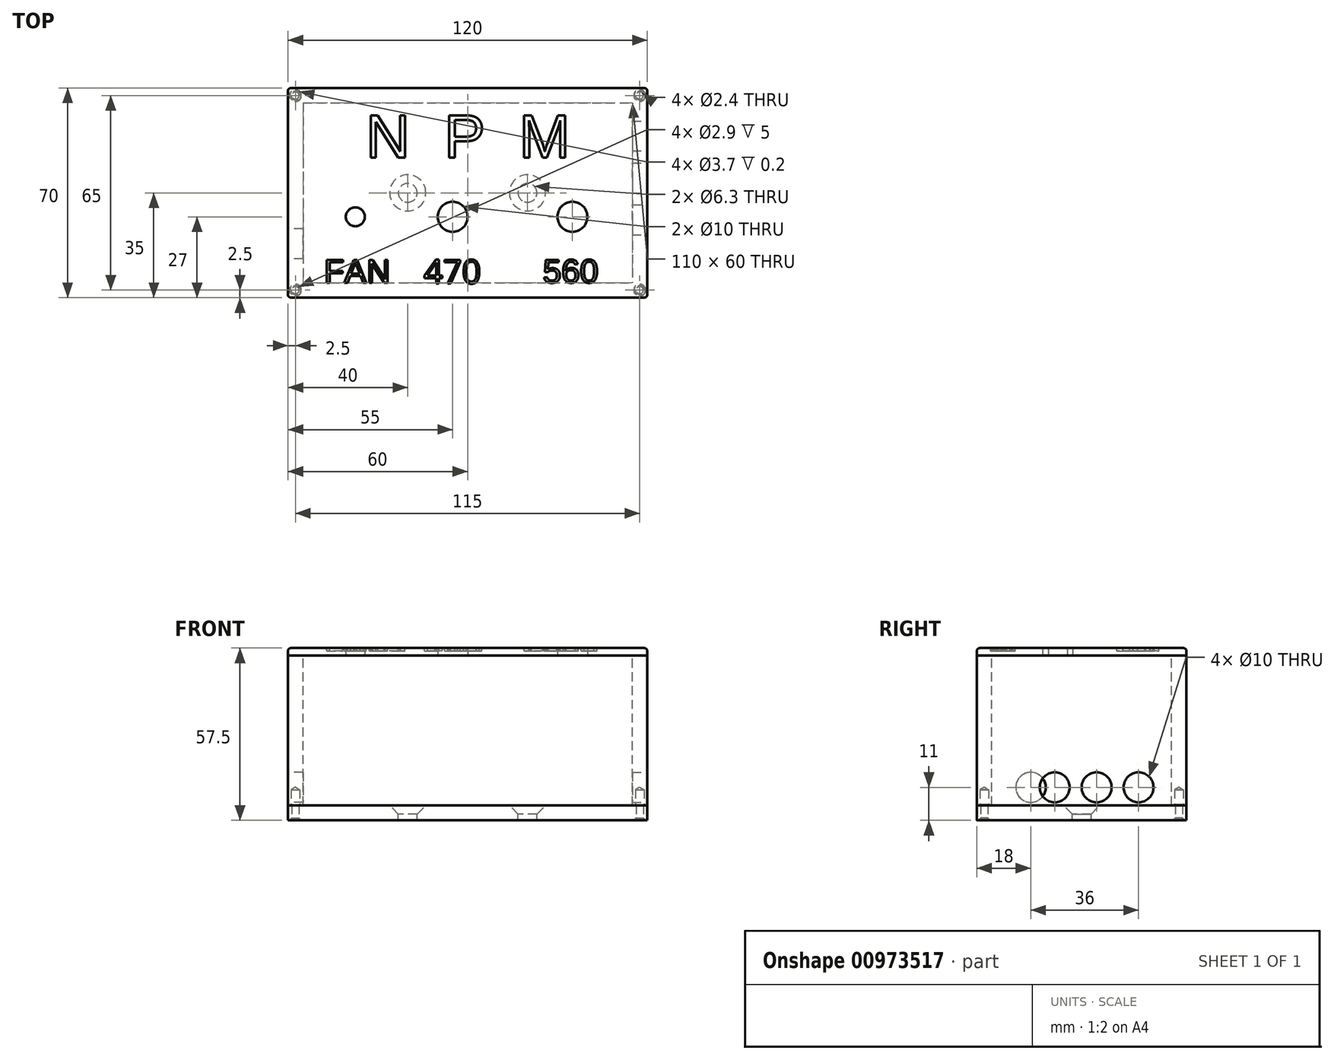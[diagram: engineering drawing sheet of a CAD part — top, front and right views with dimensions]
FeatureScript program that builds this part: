
annotation { "Feature Type Name" : "Feature", "Feature Type Description" : "" }
export const myFeature = defineFeature(function(context is Context, id is Id, definition is map)
    precondition{}
    {
        {
            var Q0;
            Q0=qCreatedBy(makeId("Top.planeOp"),FACE);
            var sketch = newSketch(context, id + "F0", { "sketchPlane" : qUnion([Q0])});
            skLineSegment(sketch, "E0.bottom", {"start": v(0, 0) * mm, "end": v(120, 0) * mm});
            skLineSegment(sketch, "E0.top", {"start": v(0, 70) * mm, "end": v(120, 70) * mm});
            skLineSegment(sketch, "E0.left", {"start": v(0, 0) * mm, "end": v(0, 70) * mm});
            skLineSegment(sketch, "E0.right", {"start": v(120, 0) * mm, "end": v(120, 70) * mm});
            skCircle(sketch, "E1", {"center": v(95, 27) * mm, "radius": 5 * mm});
            skCircle(sketch, "E2", {"center": v(55, 27) * mm, "radius": 5 * mm});
            skCircle(sketch, "E3", {"center": v(22.5, 27) * mm, "radius": 3.18 * mm});
            skLineSegment(sketch, "E4", {"start": v(5, 70) * mm, "end": v(5, 5) * mm, "construction": true});
            skLineSegment(sketch, "E5", {"start": v(5, 5) * mm, "end": v(115, 5) * mm, "construction": true});
            skLineSegment(sketch, "E6", {"start": v(115, 5) * mm, "end": v(115, 70) * mm, "construction": true});
            skLineSegment(sketch, "E7", {"start": v(0, 65) * mm, "end": v(120, 65) * mm, "construction": true});
            skLineSegment(sketch, "E8", {"start": v(5, 5) * mm, "end": v(0, 5) * mm, "construction": true});
            skLineSegment(sketch, "E9", {"start": v(115, 5) * mm, "end": v(120, 5) * mm, "construction": true});
            skPoint(sketch, "E10.endSnap0", {"position": v(5, 37.5) * mm});
            skLineSegment(sketch, "E11", {"start": v(5, 70) * mm, "end": v(115, 65) * mm, "construction": true});
            skLineSegment(sketch, "E12", {"start": v(115, 70) * mm, "end": v(5, 65) * mm, "construction": true});
            skLineSegment(sketch, "E13", {"start": v(120, 5) * mm, "end": v(0, 0) * mm, "construction": true});
            skLineSegment(sketch, "E14", {"start": v(0, 5) * mm, "end": v(120, 0) * mm, "construction": true});
            skPoint(sketch, "E15", {"position": v(60, 2.5) * mm});
            skPoint(sketch, "E16", {"position": v(60, 67.5) * mm});
            skLineSegment(sketch, "E17", {"start": v(5, 27) * mm, "end": v(115, 27) * mm, "construction": true});
            skSolve(sketch);
        }
        {
            var Q0;
            Q0=makeQuery(id+"F0.imprint","IMPRINT",FACE,{"disambiguationData":[TD([[makeQuery(id+"F0.imprint","IMPRINT",EDGE,{"derivedFrom":sQuery(id+"F0.wireOp",EDGE,"E0.bottom")}),1.0]])]});
            extrude(context, id + "F1", {"entities" : qUnion([Q0]), "depth" : 2.5 * mm, "offsetDistance" : 25 * mm});
        }
        {
            var Q0;
            Q0=makeQuery(id+"F1.opExtrude","CAP_FACE",FACE,{"disambiguationData":[OSD([sQuery(id+"F0.wireOp",EDGE,"E0.bottom"),sQuery(id+"F0.wireOp",EDGE,"E0.top"),sQuery(id+"F0.wireOp",EDGE,"E0.left"),sQuery(id+"F0.wireOp",EDGE,"E0.right"),sQuery(id+"F0.wireOp",EDGE,"E1"),sQuery(id+"F0.wireOp",EDGE,"E2"),sQuery(id+"F0.wireOp",EDGE,"E3")])],"isStart":true});
            var sketch = newSketch(context, id + "F2", { "sketchPlane" : qUnion([Q0])});
            skLineSegment(sketch, "E18.bottom", {"start": v(0, -70) * mm, "end": v(120, -70) * mm, "construction": true});
            skLineSegment(sketch, "E18.top", {"start": v(0, 0) * mm, "end": v(120, 0) * mm, "construction": true});
            skLineSegment(sketch, "E18.left", {"start": v(0, -70) * mm, "end": v(0, 0) * mm, "construction": true});
            skLineSegment(sketch, "E18.right", {"start": v(120, -70) * mm, "end": v(120, 0) * mm, "construction": true});
            skLineSegment(sketch, "E19.bottom", {"start": v(5, -65) * mm, "end": v(115, -65) * mm});
            skLineSegment(sketch, "E19.top", {"start": v(5, -5) * mm, "end": v(115, -5) * mm});
            skLineSegment(sketch, "E19.left", {"start": v(5, -65) * mm, "end": v(5, -5) * mm});
            skLineSegment(sketch, "E19.right", {"start": v(115, -65) * mm, "end": v(115, -5) * mm});
            skSolve(sketch);
        }
        {
            var Q0;
            Q0=makeQuery(id+"F2.imprint","IMPRINT",FACE,{"disambiguationData":[TD([[makeQuery(id+"F2.imprint","IMPRINT",EDGE,{"derivedFrom":sQuery(id+"F2.wireOp",EDGE,"E19.bottom")}),-1.0]])]});
            var Q1;
            Q1=makeQuery(id+"F2.imprint","IMPRINT",FACE,{"disambiguationData":[TD([[makeQuery(id+"F2.imprint","IMPRINT",EDGE,{"derivedFrom":makeQuery(id+"FxvTJw6m9mzOm3c_1.hole-0.boolean.opBoolean","INTERSECT",EDGE,{"derivedFrom":[makeQuery(id+"F1.opExtrude","CAP_FACE",FACE,{"disambiguationData":[OSD([sQuery(id+"F0.wireOp",EDGE,"E0.bottom"),sQuery(id+"F0.wireOp",EDGE,"E0.top"),sQuery(id+"F0.wireOp",EDGE,"E0.left"),sQuery(id+"F0.wireOp",EDGE,"E0.right"),sQuery(id+"F0.wireOp",EDGE,"E1"),sQuery(id+"F0.wireOp",EDGE,"E2"),sQuery(id+"F0.wireOp",EDGE,"E3")])],"isStart":true}),makeQuery(id+"FxvTJw6m9mzOm3c_1.hole-0.opRevolve","SWEPT_FACE",FACE,{"disambiguationData":[OSD([sQuery(id+"FxvTJw6m9mzOm3c_1.hole-0.sketch.wireOp",EDGE,"core_line_2")])]})]})}),1.0]])]});
            var Q2;
            Q2=makeQuery(id+"F2.imprint","IMPRINT",FACE,{"disambiguationData":[TD([[makeQuery(id+"F2.imprint","IMPRINT",EDGE,{"derivedFrom":makeQuery(id+"FxvTJw6m9mzOm3c_1.hole-1.boolean.opBoolean","INTERSECT",EDGE,{"derivedFrom":[makeQuery(id+"F1.opExtrude","CAP_FACE",FACE,{"disambiguationData":[OSD([sQuery(id+"F0.wireOp",EDGE,"E0.bottom"),sQuery(id+"F0.wireOp",EDGE,"E0.top"),sQuery(id+"F0.wireOp",EDGE,"E0.left"),sQuery(id+"F0.wireOp",EDGE,"E0.right"),sQuery(id+"F0.wireOp",EDGE,"E1"),sQuery(id+"F0.wireOp",EDGE,"E2"),sQuery(id+"F0.wireOp",EDGE,"E3")])],"isStart":true}),makeQuery(id+"FxvTJw6m9mzOm3c_1.hole-1.opRevolve","SWEPT_FACE",FACE,{"disambiguationData":[OSD([sQuery(id+"FxvTJw6m9mzOm3c_1.hole-1.sketch.wireOp",EDGE,"core_line_2")])]})]})}),1.0]])]});
            var Q3;
            Q3=makeQuery(id+"F2.imprint","IMPRINT",FACE,{"disambiguationData":[TD([[makeQuery(id+"F2.imprint","IMPRINT",EDGE,{"derivedFrom":makeQuery(id+"FxvTJw6m9mzOm3c_1.hole-2.boolean.opBoolean","INTERSECT",EDGE,{"derivedFrom":[makeQuery(id+"F1.opExtrude","CAP_FACE",FACE,{"disambiguationData":[OSD([sQuery(id+"F0.wireOp",EDGE,"E0.bottom"),sQuery(id+"F0.wireOp",EDGE,"E0.top"),sQuery(id+"F0.wireOp",EDGE,"E0.left"),sQuery(id+"F0.wireOp",EDGE,"E0.right"),sQuery(id+"F0.wireOp",EDGE,"E1"),sQuery(id+"F0.wireOp",EDGE,"E2"),sQuery(id+"F0.wireOp",EDGE,"E3")])],"isStart":true}),makeQuery(id+"FxvTJw6m9mzOm3c_1.hole-2.opRevolve","SWEPT_FACE",FACE,{"disambiguationData":[OSD([sQuery(id+"FxvTJw6m9mzOm3c_1.hole-2.sketch.wireOp",EDGE,"core_line_2")])]})]})}),1.0]])]});
            var Q4;
            Q4=makeQuery(id+"F2.imprint","IMPRINT",FACE,{"disambiguationData":[TD([[makeQuery(id+"F2.imprint","IMPRINT",EDGE,{"derivedFrom":makeQuery(id+"FxvTJw6m9mzOm3c_1.hole-3.boolean.opBoolean","INTERSECT",EDGE,{"derivedFrom":[makeQuery(id+"F1.opExtrude","CAP_FACE",FACE,{"disambiguationData":[OSD([sQuery(id+"F0.wireOp",EDGE,"E0.bottom"),sQuery(id+"F0.wireOp",EDGE,"E0.top"),sQuery(id+"F0.wireOp",EDGE,"E0.left"),sQuery(id+"F0.wireOp",EDGE,"E0.right"),sQuery(id+"F0.wireOp",EDGE,"E1"),sQuery(id+"F0.wireOp",EDGE,"E2"),sQuery(id+"F0.wireOp",EDGE,"E3")])],"isStart":true}),makeQuery(id+"FxvTJw6m9mzOm3c_1.hole-3.opRevolve","SWEPT_FACE",FACE,{"disambiguationData":[OSD([sQuery(id+"FxvTJw6m9mzOm3c_1.hole-3.sketch.wireOp",EDGE,"core_line_2")])]})]})}),1.0]])]});
            extrude(context, id + "F3", {"entities" : qUnion([Q0, Q1, Q2, Q3, Q4]), "depth" : 50 * mm, "offsetDistance" : 25 * mm});
        }
        {
            var Q0;
            Q0=makeQuery(id+"F3.opExtrude","CAP_FACE",FACE,{"disambiguationData":[OSD([sQuery(id+"F0.wireOp",EDGE,"E0.bottom"),sQuery(id+"F0.wireOp",EDGE,"E0.top"),sQuery(id+"F0.wireOp",EDGE,"E0.left"),sQuery(id+"F0.wireOp",EDGE,"E0.right"),sQuery(id+"F2.wireOp",EDGE,"E19.bottom"),sQuery(id+"F2.wireOp",EDGE,"E19.top"),sQuery(id+"F2.wireOp",EDGE,"E19.left"),sQuery(id+"F2.wireOp",EDGE,"E19.right")])],"isStart":false});
            var sketch = newSketch(context, id + "F4", { "sketchPlane" : qUnion([Q0])});
            skLineSegment(sketch, "E20.bottom", {"start": v(0, 0) * mm, "end": v(120, 0) * mm});
            skLineSegment(sketch, "E20.top", {"start": v(0, -70) * mm, "end": v(120, -70) * mm});
            skLineSegment(sketch, "E20.left", {"start": v(0, 0) * mm, "end": v(0, -70) * mm});
            skLineSegment(sketch, "E20.right", {"start": v(120, 0) * mm, "end": v(120, -70) * mm});
            skLineSegment(sketch, "E21.bottom", {"start": v(5, -5) * mm, "end": v(115, -5) * mm, "construction": true});
            skLineSegment(sketch, "E21.top", {"start": v(5, -65) * mm, "end": v(115, -65) * mm, "construction": true});
            skLineSegment(sketch, "E21.left", {"start": v(5, -5) * mm, "end": v(5, -65) * mm, "construction": true});
            skLineSegment(sketch, "E21.right", {"start": v(115, -5) * mm, "end": v(115, -65) * mm, "construction": true});
            skSolve(sketch);
        }
        {
            var Q0;
            Q0=makeQuery(id+"F4.imprint","IMPRINT",FACE,{"disambiguationData":[TD([[makeQuery(id+"F4.imprint","IMPRINT",EDGE,{"derivedFrom":sQuery(id+"F4.wireOp",EDGE,"E20.bottom")}),-1.0]])]});
            var Q1;
            Q1=makeQuery(id+"F4.imprint","IMPRINT",FACE,{"disambiguationData":[TD([[makeQuery(id+"F4.imprint","IMPRINT",EDGE,{"derivedFrom":makeQuery(id+"F3.opExtrude","CAP_EDGE",EDGE,{"disambiguationData":[OSD([sQuery(id+"F2.wireOp",EDGE,"E19.bottom")])],"isStart":false})}),1.0]])]});
            extrude(context, id + "F5", {"entities" : qUnion([Q0, Q1]), "depth" : 5 * mm, "offsetDistance" : 25 * mm});
        }
        {
            var Q0;
            Q0=makeQuery(id+"F5.opExtrude","CAP_FACE",FACE,{"disambiguationData":[OSD([sQuery(id+"F4.wireOp",EDGE,"E20.bottom"),sQuery(id+"F4.wireOp",EDGE,"E20.top"),sQuery(id+"F4.wireOp",EDGE,"E20.left"),sQuery(id+"F4.wireOp",EDGE,"E20.right")])],"isStart":false});
            var sketch = newSketch(context, id + "F6", { "sketchPlane" : qUnion([Q0])});
            skLineSegment(sketch, "E22.bottom", {"start": v(0, -70) * mm, "end": v(120, -70) * mm, "construction": true});
            skLineSegment(sketch, "E22.top", {"start": v(0, 0) * mm, "end": v(120, 0) * mm, "construction": true});
            skLineSegment(sketch, "E22.left", {"start": v(0, -70) * mm, "end": v(0, 0) * mm, "construction": true});
            skLineSegment(sketch, "E22.right", {"start": v(120, -70) * mm, "end": v(120, 0) * mm, "construction": true});
            skLineSegment(sketch, "E23.bottom", {"start": v(5, -65) * mm, "end": v(115, -65) * mm, "construction": true});
            skLineSegment(sketch, "E23.top", {"start": v(5, -5) * mm, "end": v(115, -5) * mm, "construction": true});
            skLineSegment(sketch, "E23.left", {"start": v(5, -65) * mm, "end": v(5, -5) * mm, "construction": true});
            skLineSegment(sketch, "E23.right", {"start": v(115, -65) * mm, "end": v(115, -5) * mm, "construction": true});
            skLineSegment(sketch, "E24", {"start": v(5, -5) * mm, "end": v(0, 0) * mm, "construction": true});
            skLineSegment(sketch, "E25", {"start": v(115, -5) * mm, "end": v(120, 0) * mm, "construction": true});
            skLineSegment(sketch, "E26", {"start": v(115, -65) * mm, "end": v(120, -70) * mm, "construction": true});
            skLineSegment(sketch, "E27", {"start": v(5, -65) * mm, "end": v(0, -70) * mm, "construction": true});
            skPoint(sketch, "E28", {"position": v(2.5, -2.5) * mm});
            skPoint(sketch, "E29", {"position": v(117.5, -2.5) * mm});
            skPoint(sketch, "E30", {"position": v(117.5, -67.5) * mm});
            skPoint(sketch, "E31", {"position": v(2.5, -67.5) * mm});
            skSolve(sketch);
        }
        {
            var Q0;
            Q0=sQuery(id+"F6.wireOp",VERTEX,"E28");
            var Q1;
            Q1=sQuery(id+"F6.wireOp",VERTEX,"E31");
            var Q2;
            Q2=sQuery(id+"F6.wireOp",VERTEX,"E30");
            var Q3;
            Q3=sQuery(id+"F6.wireOp",VERTEX,"E29");
            var Q4;
            Q4=makeQuery(id+"F3.opExtrude","SWEPT_BODY",BODY,{"disambiguationData":[OSD([sQuery(id+"F0.wireOp",EDGE,"E0.bottom"),sQuery(id+"F0.wireOp",EDGE,"E0.top"),sQuery(id+"F0.wireOp",EDGE,"E0.left"),sQuery(id+"F0.wireOp",EDGE,"E0.right"),sQuery(id+"F2.wireOp",EDGE,"E19.bottom"),sQuery(id+"F2.wireOp",EDGE,"E19.top"),sQuery(id+"F2.wireOp",EDGE,"E19.left"),sQuery(id+"F2.wireOp",EDGE,"E19.right")])]});
            var Q5;
            Q5=makeQuery(id+"F5.opExtrude","SWEPT_BODY",BODY,{"disambiguationData":[OSD([sQuery(id+"F4.wireOp",EDGE,"E20.bottom"),sQuery(id+"F4.wireOp",EDGE,"E20.top"),sQuery(id+"F4.wireOp",EDGE,"E20.left"),sQuery(id+"F4.wireOp",EDGE,"E20.right")])]});
            hole(context, id + "F7", {"style" : HoleStyle.C_SINK, "endStyle" : HoleEndStyle.BLIND, "holeDiameter" : 2.4 * mm, "cSinkDiameter" : 4 * mm, "cSinkAngle" : 90 * degree, "majorDiameter" : 5 * mm, "holeDepth" : 5 * mm, "isTappedThrough" : true, "tappedDepth" : 12 * mm, "tapClearance" : 3, "locations" : qUnion([Q0, Q1, Q2, Q3]), "scope" : qUnion([Q4, Q5])});
        }
        {
            var Q0;
            Q0=makeQuery(id+"F3.opExtrude","CAP_FACE",FACE,{"disambiguationData":[OSD([sQuery(id+"F0.wireOp",EDGE,"E0.bottom"),sQuery(id+"F0.wireOp",EDGE,"E0.top"),sQuery(id+"F0.wireOp",EDGE,"E0.left"),sQuery(id+"F0.wireOp",EDGE,"E0.right"),sQuery(id+"F2.wireOp",EDGE,"E19.bottom"),sQuery(id+"F2.wireOp",EDGE,"E19.top"),sQuery(id+"F2.wireOp",EDGE,"E19.left"),sQuery(id+"F2.wireOp",EDGE,"E19.right")])],"isStart":false});
            var sketch = newSketch(context, id + "F8", { "sketchPlane" : qUnion([Q0])});
            skPoint(sketch, "E32", {"position": v(2.5, -2.5) * mm});
            skPoint(sketch, "E33", {"position": v(2.5, -67.5) * mm});
            skPoint(sketch, "E34", {"position": v(117.5, -67.5) * mm});
            skPoint(sketch, "E35", {"position": v(117.5, -2.5) * mm});
            skSolve(sketch);
        }
        {
            var Q0;
            Q0=sQuery(id+"F8.wireOp",VERTEX,"E32");
            var Q1;
            Q1=sQuery(id+"F8.wireOp",VERTEX,"E33");
            var Q2;
            Q2=sQuery(id+"F8.wireOp",VERTEX,"E34");
            var Q3;
            Q3=sQuery(id+"F8.wireOp",VERTEX,"E35");
            var Q4;
            Q4=makeQuery(id+"F3.opExtrude","SWEPT_BODY",BODY,{"disambiguationData":[OSD([sQuery(id+"F0.wireOp",EDGE,"E0.bottom"),sQuery(id+"F0.wireOp",EDGE,"E0.top"),sQuery(id+"F0.wireOp",EDGE,"E0.left"),sQuery(id+"F0.wireOp",EDGE,"E0.right"),sQuery(id+"F2.wireOp",EDGE,"E19.bottom"),sQuery(id+"F2.wireOp",EDGE,"E19.top"),sQuery(id+"F2.wireOp",EDGE,"E19.left"),sQuery(id+"F2.wireOp",EDGE,"E19.right")])]});
            hole(context, id + "F9", {"style" : HoleStyle.C_BORE, "endStyle" : HoleEndStyle.BLIND, "holeDiameter" : 2.9 * mm, "cBoreDiameter" : 3.7 * mm, "cBoreDepth" : .2 * mm, "majorDiameter" : 5 * mm, "holeDepth" : 5.2 * mm, "isTappedThrough" : true, "tappedDepth" : 12 * mm, "tapClearance" : 3, "locations" : qUnion([Q0, Q1, Q2, Q3]), "scope" : qUnion([Q4])});
        }
        {
            var Q0;
            Q0=makeQuery(id+"F1.opExtrude","CAP_EDGE",EDGE,{"disambiguationData":[OSD([sQuery(id+"F0.wireOp",EDGE,"E0.bottom")])],"isStart":false});
            var Q1;
            Q1=makeQuery(id+"F1.opExtrude","CAP_EDGE",EDGE,{"disambiguationData":[OSD([sQuery(id+"F0.wireOp",EDGE,"E0.left")])],"isStart":false});
            var Q2;
            Q2=makeQuery(id+"F1.opExtrude","CAP_EDGE",EDGE,{"disambiguationData":[OSD([sQuery(id+"F0.wireOp",EDGE,"E0.top")])],"isStart":false});
            var Q3;
            Q3=makeQuery(id+"F1.opExtrude","CAP_EDGE",EDGE,{"disambiguationData":[OSD([sQuery(id+"F0.wireOp",EDGE,"E0.right")])],"isStart":false});
            var Q4;
            Q4=makeQuery(id+"F3.opExtrude","SWEPT_EDGE",EDGE,{"disambiguationData":[OSD([sQuery(id+"F0.wireOp",EDGE,"E0.bottom"),sQuery(id+"F0.wireOp",EDGE,"E0.right")])]});
            var Q5;
            Q5=makeQuery(id+"F3.opExtrude","SWEPT_EDGE",EDGE,{"disambiguationData":[OSD([sQuery(id+"F0.wireOp",EDGE,"E0.bottom"),sQuery(id+"F0.wireOp",EDGE,"E0.left")])]});
            var Q6;
            Q6=makeQuery(id+"F1.opExtrude","SWEPT_EDGE",EDGE,{"disambiguationData":[OSD([sQuery(id+"F0.wireOp",EDGE,"E0.bottom"),sQuery(id+"F0.wireOp",EDGE,"E0.left")])]});
            var Q7;
            Q7=makeQuery(id+"F1.opExtrude","SWEPT_EDGE",EDGE,{"disambiguationData":[OSD([sQuery(id+"F0.wireOp",EDGE,"E0.bottom"),sQuery(id+"F0.wireOp",EDGE,"E0.right")])]});
            var Q8;
            Q8=makeQuery(id+"F3.opExtrude","SWEPT_EDGE",EDGE,{"disambiguationData":[OSD([sQuery(id+"F0.wireOp",EDGE,"E0.top"),sQuery(id+"F0.wireOp",EDGE,"E0.right")])]});
            var Q9;
            Q9=makeQuery(id+"F1.opExtrude","SWEPT_EDGE",EDGE,{"disambiguationData":[OSD([sQuery(id+"F0.wireOp",EDGE,"E0.top"),sQuery(id+"F0.wireOp",EDGE,"E0.right")])]});
            var Q10;
            Q10=makeQuery(id+"F3.opExtrude","SWEPT_EDGE",EDGE,{"disambiguationData":[OSD([sQuery(id+"F0.wireOp",EDGE,"E0.top"),sQuery(id+"F0.wireOp",EDGE,"E0.left")])]});
            var Q11;
            Q11=makeQuery(id+"F1.opExtrude","SWEPT_EDGE",EDGE,{"disambiguationData":[OSD([sQuery(id+"F0.wireOp",EDGE,"E0.top"),sQuery(id+"F0.wireOp",EDGE,"E0.left")])]});
            var Q12;
            Q12=makeQuery(id+"F5.opExtrude","SWEPT_EDGE",EDGE,{"disambiguationData":[OSD([sQuery(id+"F4.wireOp",EDGE,"E20.top"),sQuery(id+"F4.wireOp",EDGE,"E20.left")])]});
            var Q13;
            Q13=makeQuery(id+"F5.opExtrude","SWEPT_EDGE",EDGE,{"disambiguationData":[OSD([sQuery(id+"F4.wireOp",EDGE,"E20.bottom"),sQuery(id+"F4.wireOp",EDGE,"E20.left")])]});
            var Q14;
            Q14=makeQuery(id+"F5.opExtrude","SWEPT_EDGE",EDGE,{"disambiguationData":[OSD([sQuery(id+"F4.wireOp",EDGE,"E20.top"),sQuery(id+"F4.wireOp",EDGE,"E20.right")])]});
            var Q15;
            Q15=makeQuery(id+"F5.opExtrude","SWEPT_EDGE",EDGE,{"disambiguationData":[OSD([sQuery(id+"F4.wireOp",EDGE,"E20.bottom"),sQuery(id+"F4.wireOp",EDGE,"E20.right")])]});
            fillet(context, id + "F10", {"entities" : qUnion([Q0, Q1, Q2, Q3, Q4, Q5, Q6, Q7, Q8, Q9, Q10, Q11, Q12, Q13, Q14, Q15]), "radius" : 1 * mm, "tangentPropagation" : true, "allowEdgeOverflow" : false});
        }
        {
            var Q0;
            Q0=makeQuery(id+"F3.opExtrude","SWEPT_FACE",FACE,{"disambiguationData":[OSD([sQuery(id+"F0.wireOp",EDGE,"E0.left")])]});
            var sketch = newSketch(context, id + "F11", { "sketchPlane" : qUnion([Q0])});
            skCircle(sketch, "E36", {"center": v(-18, -44) * mm, "radius": 5 * mm});
            skLineSegment(sketch, "E37", {"start": v(-35, -50) * mm, "end": v(-35, 0) * mm, "construction": true});
            skLineSegment(sketch, "E38", {"start": v(-35, 0) * mm, "end": v(-1, -50) * mm, "construction": true});
            skLineSegment(sketch, "E39", {"start": v(-18, -25) * mm, "end": v(-18, -50) * mm, "construction": true});
            skLineSegment(sketch, "E40", {"start": v(-18, -50) * mm, "end": v(-18, 0) * mm, "construction": true});
            skSolve(sketch);
        }
        {
            var Q0;
            Q0=makeQuery(id+"F11.imprint","IMPRINT",FACE,{"disambiguationData":[TD([[makeQuery(id+"F11.imprint","IMPRINT",EDGE,{"derivedFrom":sQuery(id+"F11.wireOp",EDGE,"E36")}),1.0]])]});
            extrude(context, id + "F12", {"entities" : qUnion([Q0]), "operationType" : NewBodyOperationType.REMOVE, "endBound" : BoundingType.UP_TO_NEXT, "oppositeDirection" : true, "depth" : 25 * mm, "offsetDistance" : 25 * mm});
        }
        {
            var Q0;
            Q0=makeQuery(id+"F3.opExtrude","SWEPT_FACE",FACE,{"disambiguationData":[OSD([sQuery(id+"F0.wireOp",EDGE,"E0.right")])]});
            var sketch = newSketch(context, id + "F13", { "sketchPlane" : qUnion([Q0])});
            skLineSegment(sketch, "E41", {"start": v(1, -44) * mm, "end": v(69, -44) * mm, "construction": true});
            skCircle(sketch, "E42", {"center": v(26, -44) * mm, "radius": 5 * mm});
            skCircle(sketch, "E43", {"center": v(40, -44) * mm, "radius": 5 * mm});
            skCircle(sketch, "E44", {"center": v(54, -44) * mm, "radius": 5 * mm});
            skSolve(sketch);
        }
        {
            var Q0;
            Q0=makeQuery(id+"F13.imprint","IMPRINT",FACE,{"disambiguationData":[TD([[makeQuery(id+"F13.imprint","IMPRINT",EDGE,{"derivedFrom":sQuery(id+"F13.wireOp",EDGE,"E42")}),1.0]])]});
            var Q1;
            Q1=makeQuery(id+"F13.imprint","IMPRINT",FACE,{"disambiguationData":[TD([[makeQuery(id+"F13.imprint","IMPRINT",EDGE,{"derivedFrom":sQuery(id+"F13.wireOp",EDGE,"E43")}),1.0]])]});
            var Q2;
            Q2=makeQuery(id+"F13.imprint","IMPRINT",FACE,{"disambiguationData":[TD([[makeQuery(id+"F13.imprint","IMPRINT",EDGE,{"derivedFrom":sQuery(id+"F13.wireOp",EDGE,"E44")}),1.0]])]});
            extrude(context, id + "F14", {"entities" : qUnion([Q0, Q1, Q2]), "operationType" : NewBodyOperationType.REMOVE, "endBound" : BoundingType.UP_TO_NEXT, "oppositeDirection" : true, "depth" : 25 * mm, "offsetDistance" : 25 * mm});
        }
        {
            var Q0;
            Q0=makeQuery(id+"F10.opFillet","SPLIT",FACE,{"disambiguationData":[OD(4.0)],"derivedFrom":makeQuery(id+"F1.opExtrude","CAP_FACE",FACE,{"disambiguationData":[OSD([sQuery(id+"F0.wireOp",EDGE,"E0.bottom"),sQuery(id+"F0.wireOp",EDGE,"E0.top"),sQuery(id+"F0.wireOp",EDGE,"E0.left"),sQuery(id+"F0.wireOp",EDGE,"E0.right"),sQuery(id+"F0.wireOp",EDGE,"E1"),sQuery(id+"F0.wireOp",EDGE,"E2"),sQuery(id+"F0.wireOp",EDGE,"E3")])],"isStart":false})});
            var sketch = newSketch(context, id + "F15", { "sketchPlane" : qUnion([Q0])});
            skLineSegment(sketch, "E45.bottom", {"start": v(1, 61.5) * mm, "end": v(119, 61.5) * mm, "construction": true});
            skLineSegment(sketch, "E45.top", {"start": v(1, 46.75) * mm, "end": v(119, 46.75) * mm, "construction": true});
            skLineSegment(sketch, "E45.left", {"start": v(1, 61.5) * mm, "end": v(1, 46.75) * mm, "construction": true});
            skLineSegment(sketch, "E45.right", {"start": v(119, 61.5) * mm, "end": v(119, 46.75) * mm, "construction": true});
            skLineSegment(sketch, "E46", {"start": v(60, 61.5) * mm, "end": v(60, 46.75) * mm, "construction": true});
            skLineSegment(sketch, "E47.bottom", {"start": v(77.87, 61.5) * mm, "end": v(25.99, 61.5) * mm, "construction": true});
            skLineSegment(sketch, "E47.top", {"start": v(94.01, 46.75) * mm, "end": v(42.13, 46.75) * mm, "construction": true});
            skLineSegment(sketch, "E47.left", {"start": v(77.87, 61.5) * mm, "end": v(94.01, 46.75) * mm, "construction": true});
            skLineSegment(sketch, "E47.right", {"start": v(25.99, 61.5) * mm, "end": v(42.13, 46.75) * mm, "construction": true});
            skPoint(sketch, "E47.middle", {"position": v(60, 54.12) * mm});
            skText(sketch, "E48", { "text": "N  P  M", "fontName": "Arimo-Regular.ttf"});
            const initialGuessF15  = {"E48": [0.02599, 0.04675, 1, 0, 0.01475]};
            skSetInitialGuess(sketch, initialGuessF15);
            skSolve(sketch);
        }
        {
            var Q0;
            Q0 = qSketchRegion(id + "F15", true);
            extrude(context, id + "F16", {"entities" : qUnion([Q0]), "operationType" : NewBodyOperationType.REMOVE, "oppositeDirection" : true, "depth" : 1 * mm, "offsetDistance" : 25 * mm});
        }
        {
            var Q0;
            {var subQ0=sQuery(id+"F0.wireOp",EDGE,"E0.right");var subQ1=sQuery(id+"F0.wireOp",EDGE,"E0.left");var subQ2=sQuery(id+"F0.wireOp",EDGE,"E0.top");var subQ3=sQuery(id+"F0.wireOp",EDGE,"E0.bottom");var subQ4=sQuery(id+"F0.wireOp",EDGE,"E3");var subQ5=sQuery(id+"F0.wireOp",EDGE,"E2");var subQ6=sQuery(id+"F0.wireOp",EDGE,"E1");Q0=makeQuery(id+"F16.boolean.opBoolean","SPLIT",FACE,{"disambiguationData":[TD([makeQuery(id+"F1.opExtrude","SWEPT_FACE",FACE,{"disambiguationData":[OSD([subQ6])]})])],"derivedFrom":makeQuery(id+"F1.opExtrude","CAP_FACE",FACE,{"disambiguationData":[OSD([subQ3,subQ2,subQ1,subQ0,subQ6,subQ5,subQ4])],"isStart":false})});}
            var sketch = newSketch(context, id + "F17", { "sketchPlane" : qUnion([Q0])});
            skText(sketch, "E49", { "text": "FAN", "fontName": "Arimo-Regular.ttf"});
            skText(sketch, "E50", { "text": "560", "fontName": "Arimo-Regular.ttf"});
            skText(sketch, "E51", { "text": "470\n", "fontName": "OpenSans-Regular.ttf"});
            const initialGuessF17  = {"E49": [0.012, 0.005, 1, 0, 0.008], "E50": [0.08513, 0.005, 1, 0, 0.008], "E51": [0.0454, 0.00472, 1, 0, 0.008]};
            skSetInitialGuess(sketch, initialGuessF17);
            skSolve(sketch);
        }
        {
            var Q0;
            Q0 = qSketchRegion(id + "F17", true);
            extrude(context, id + "F18", {"entities" : qUnion([Q0]), "operationType" : NewBodyOperationType.REMOVE, "oppositeDirection" : true, "depth" : 1 * mm, "offsetDistance" : 25 * mm});
        }
        {
            var Q0;
            Q0=makeQuery(id+"F5.opExtrude","CAP_FACE",FACE,{"disambiguationData":[OSD([sQuery(id+"F4.wireOp",EDGE,"E20.bottom"),sQuery(id+"F4.wireOp",EDGE,"E20.top"),sQuery(id+"F4.wireOp",EDGE,"E20.left"),sQuery(id+"F4.wireOp",EDGE,"E20.right")])],"isStart":true});
            var sketch = newSketch(context, id + "F19", { "sketchPlane" : qUnion([Q0])});
            skLineSegment(sketch, "E52", {"start": v(60, 70) * mm, "end": v(60, 0) * mm, "construction": true});
            skLineSegment(sketch, "E53", {"start": v(120, 35) * mm, "end": v(0, 35) * mm, "construction": true});
            skPoint(sketch, "E54", {"position": v(40, 35) * mm});
            skPoint(sketch, "E55", {"position": v(80, 35) * mm});
            skSolve(sketch);
        }
        {
            var Q0;
            Q0=sQuery(id+"F19.wireOp",VERTEX,"E54");
            var Q1;
            Q1=sQuery(id+"F19.wireOp",VERTEX,"E55");
            var Q2;
            Q2=makeQuery(id+"F5.opExtrude","SWEPT_BODY",BODY,{"disambiguationData":[OSD([sQuery(id+"F4.wireOp",EDGE,"E20.bottom"),sQuery(id+"F4.wireOp",EDGE,"E20.top"),sQuery(id+"F4.wireOp",EDGE,"E20.left"),sQuery(id+"F4.wireOp",EDGE,"E20.right")])]});
            hole(context, id + "F20", {"style" : HoleStyle.C_SINK, "endStyle" : HoleEndStyle.BLIND, "holeDiameter" : 6.3 * mm, "cSinkDiameter" : 12.1 * mm, "cSinkAngle" : 90 * degree, "majorDiameter" : 5 * mm, "holeDepth" : 5.2 * mm, "isTappedThrough" : true, "tappedDepth" : 12 * mm, "tapClearance" : 3, "locations" : qUnion([Q0, Q1]), "scope" : qUnion([Q2])});
        }
    });
